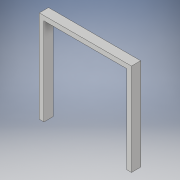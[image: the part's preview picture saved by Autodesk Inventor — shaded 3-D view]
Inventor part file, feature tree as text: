
AUTODESK INVENTOR PART (.ipt)
format: ipt  version: 2017 (Build 210142000, 142)  size: 99,328 bytes
history: native  units: in
note: dims shown in document units (in); Inventor stores cm internally (conversion verified against a paired STEP export)
features: extrude x1, sketch x1
ambient origin geometry x8: Origin, YZ Plane, XZ Plane, XY Plane, X Axis, Y Axis, Z Axis, Center Point
bodies: Solid1 (feature_tree)
feature tree (2):
  extrude  "Extrusion1"  Depth=5.0in
  sketch  "Sketch1"  dims[d0=5.0in d1=5.0in d2=0.25in d3=4.75in d4=4.5in d5=0.5in d6=0.0in]
